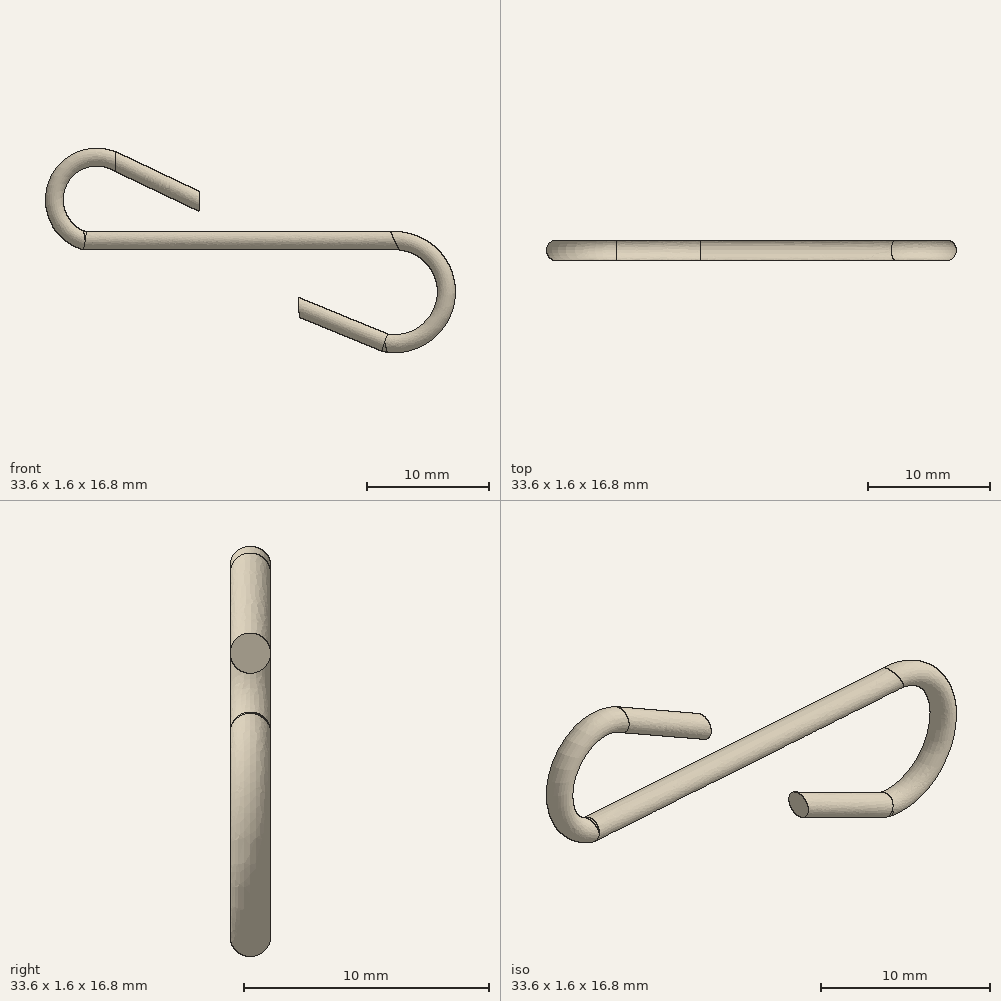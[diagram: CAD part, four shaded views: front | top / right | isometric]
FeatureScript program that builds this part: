
annotation { "Feature Type Name" : "Feature", "Feature Type Description" : "" }
export const myFeature = defineFeature(function(context is Context, id is Id, definition is map)
    precondition{}
    {
        {
            var Q0;
            Q0=qCreatedBy(makeId("Front.planeOp"),FACE);
            var sketch = newSketch(context, id + "F0", { "sketchPlane" : qUnion([Q0])});
            skLineSegment(sketch, "E0", {"start": v(-34.56, -1.72) * mm, "end": v(-9.16, -1.72) * mm});
            skLineSegment(sketch, "E1", {"start": v(-25.2, 1.54) * mm, "end": v(-32.07, 4.8) * mm});
            skLineSegment(sketch, "E2", {"start": v(-17.05, -7.14) * mm, "end": v(-10, -10.03) * mm});
            skArc(sketch, "E3", {"start": v(-32.07, 4.8) * mm, "mid": v(-36.85, 2.9) * mm, "end": v(-34.56, -1.72) * mm});
            skArc(sketch, "E4", {"start": v(-10, -10.03) * mm, "mid": v(-4.99, -6.34) * mm, "end": v(-9.16, -1.72) * mm});
            skSolve(sketch);
        }
        {
            var Q0;
            Q0=sQuery(id+"F0.wireOp",VERTEX,"E1.start");
            var Q1;
            Q1=qCreatedBy(makeId("Right.planeOp"),FACE);
            cPlane(context, id + "F1", {"entities" : qUnion([Q0, Q1]), "cplaneType" : CPlaneType.PLANE_POINT, "offset" : 25.4 * mm, "width" : 152.4 * mm, "height" : 152.4 * mm});
        }
        {
            var Q0;
            Q0=qCreatedBy(id+"F1.planeOp",FACE);
            var sketch = newSketch(context, id + "F2", { "sketchPlane" : qUnion([Q0])});
            skCircle(sketch, "E5", {"center": v(0, 1.52) * mm, "radius": 0.83 * mm});
            skSolve(sketch);
        }
        {
            var Q0;
            Q0=makeQuery(id+"F2.imprint","IMPRINT",FACE,{"disambiguationData":[TD([[makeQuery(id+"F2.imprint","IMPRINT",EDGE,{"derivedFrom":sQuery(id+"F2.wireOp",EDGE,"E5")}),1.0]])]});
            var Q1;
            Q1=sQuery(id+"F0.wireOp",EDGE,"E1");
            var Q2;
            Q2=sQuery(id+"F0.wireOp",EDGE,"E3");
            var Q3;
            Q3=sQuery(id+"F0.wireOp",EDGE,"E0");
            var Q4;
            Q4=sQuery(id+"F0.wireOp",EDGE,"E4");
            var Q5;
            Q5=sQuery(id+"F0.wireOp",EDGE,"E2");
            sweep(context, id + "F3", {"profiles" : qUnion([Q0]), "path" : qUnion([Q1, Q2, Q3, Q4, Q5])});
        }
    });
